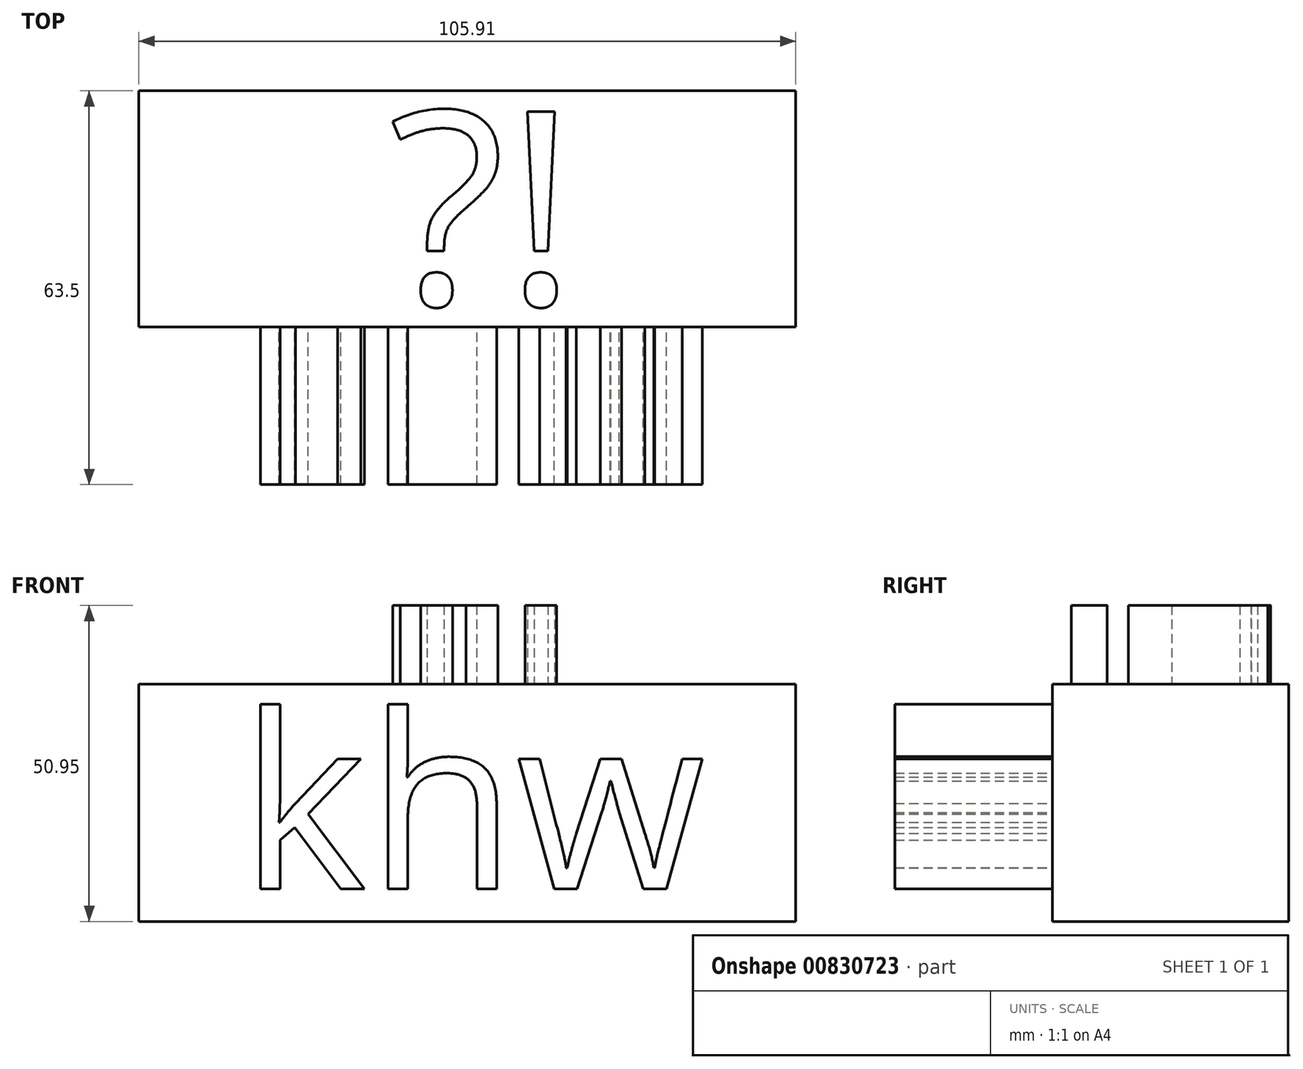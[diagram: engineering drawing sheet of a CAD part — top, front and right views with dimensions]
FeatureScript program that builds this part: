
annotation { "Feature Type Name" : "Feature", "Feature Type Description" : "" }
export const myFeature = defineFeature(function(context is Context, id is Id, definition is map)
    precondition{}
    {
        {
            var Q0;
            Q0=qCreatedBy(makeId("Front.planeOp"),FACE);
            var sketch = newSketch(context, id + "F0", { "sketchPlane" : qUnion([Q0])});
            skLineSegment(sketch, "E0.bottom", {"start": v(0, 0) * mm, "end": v(105.91, 0) * mm});
            skLineSegment(sketch, "E0.top", {"start": v(0, 38.25) * mm, "end": v(105.91, 38.25) * mm});
            skLineSegment(sketch, "E0.left", {"start": v(0, 0) * mm, "end": v(0, 38.25) * mm});
            skLineSegment(sketch, "E0.right", {"start": v(105.91, 0) * mm, "end": v(105.91, 38.25) * mm});
            skSolve(sketch);
        }
        {
            var Q0;
            Q0=makeQuery(id+"F0.imprint","IMPRINT",FACE,{"disambiguationData":[TD([[makeQuery(id+"F0.imprint","IMPRINT",EDGE,{"derivedFrom":sQuery(id+"F0.wireOp",EDGE,"E0.bottom")}),1.0]])]});
            extrude(context, id + "F1", {"entities" : qUnion([Q0]), "depth" : 38.1 * mm, "offsetDistance" : 25.4 * mm});
        }
        {
            var Q0;
            Q0=makeQuery(id+"F1.opExtrude","CAP_FACE",FACE,{"disambiguationData":[OSD([sQuery(id+"F0.wireOp",EDGE,"E0.bottom"),sQuery(id+"F0.wireOp",EDGE,"E0.top"),sQuery(id+"F0.wireOp",EDGE,"E0.left"),sQuery(id+"F0.wireOp",EDGE,"E0.right")])],"isStart":false});
            var sketch = newSketch(context, id + "F2", { "sketchPlane" : qUnion([Q0])});
            skText(sketch, "E1", { "text": "khw", "fontName": "OpenSans-Regular.ttf"});
            const initialGuessF2  = {"E1": [0.01624, 0.00525, 1, 0, 0.0282]};
            skSetInitialGuess(sketch, initialGuessF2);
            skSolve(sketch);
        }
        {
            var Q0;
            Q0 = qSketchRegion(id + "F2", true);
            extrude(context, id + "F3", {"entities" : qUnion([Q0]), "operationType" : NewBodyOperationType.ADD, "depth" : 25.4 * mm, "offsetDistance" : 25.4 * mm});
        }
        {
            var Q0;
            Q0=makeQuery(id+"F1.opExtrude","SWEPT_FACE",FACE,{"disambiguationData":[OSD([sQuery(id+"F0.wireOp",EDGE,"E0.top")])]});
            var sketch = newSketch(context, id + "F4", { "sketchPlane" : qUnion([Q0])});
            skText(sketch, "E2", { "text": "?!", "fontName": "OpenSans-Regular.ttf"});
            const initialGuessF4  = {"E2": [0.04034, -0.03442, 1, 0, 0.03134]};
            skSetInitialGuess(sketch, initialGuessF4);
            skSolve(sketch);
        }
        {
            var Q0;
            Q0 = qSketchRegion(id + "F4", true);
            extrude(context, id + "F5", {"entities" : qUnion([Q0]), "operationType" : NewBodyOperationType.ADD, "depth" : 12.7 * mm, "offsetDistance" : 25.4 * mm});
        }
    });
